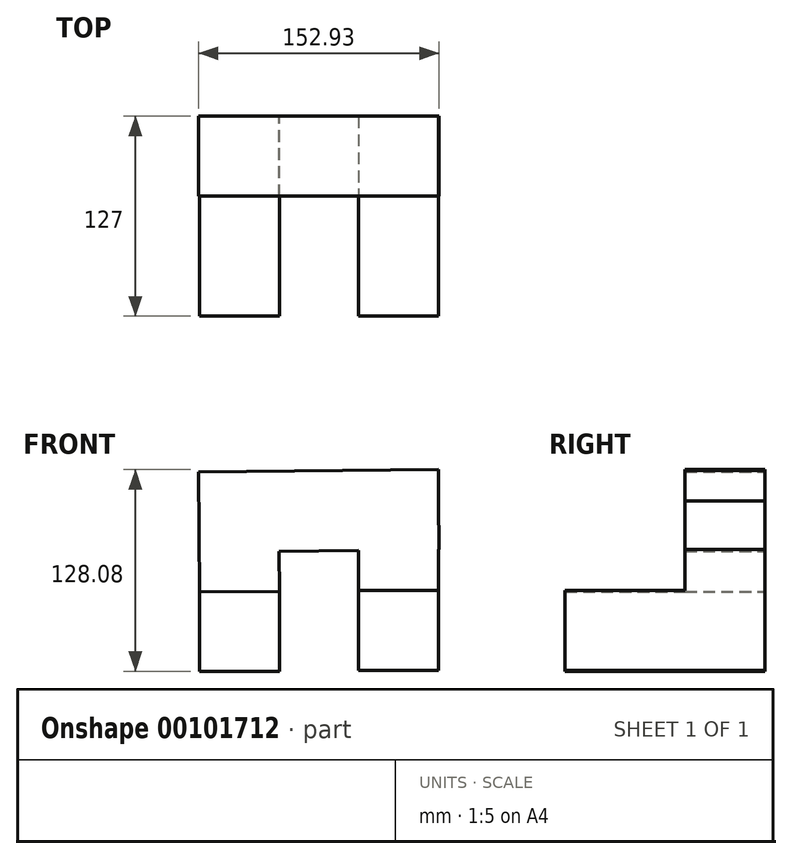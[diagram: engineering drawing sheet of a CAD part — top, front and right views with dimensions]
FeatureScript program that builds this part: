
annotation { "Feature Type Name" : "Feature", "Feature Type Description" : "" }
export const myFeature = defineFeature(function(context is Context, id is Id, definition is map)
    precondition{}
    {
        {
            var Q0;
            Q0=qCreatedBy(makeId("Front.planeOp"),FACE);
            var sketch = newSketch(context, id + "F0", { "sketchPlane" : qUnion([Q0])});
            skLineSegment(sketch, "E0", {"start": v(-79.81, 16.15) * mm, "end": v(-79.81, -34.1) * mm});
            skLineSegment(sketch, "E1", {"start": v(-79.81, -34.1) * mm, "end": v(-29.02, -34.1) * mm});
            skLineSegment(sketch, "E2", {"start": v(-29.02, -34.1) * mm, "end": v(-29.02, 16.7) * mm});
            skLineSegment(sketch, "E3", {"start": v(-29.02, 16.7) * mm, "end": v(-79.81, 16.15) * mm});
            skLineSegment(sketch, "E4", {"start": v(21.18, 17.14) * mm, "end": v(21.18, -33.66) * mm});
            skLineSegment(sketch, "E5", {"start": v(21.18, -33.66) * mm, "end": v(71.98, -33.66) * mm});
            skLineSegment(sketch, "E6", {"start": v(71.98, -33.66) * mm, "end": v(71.98, 17.14) * mm});
            skLineSegment(sketch, "E7", {"start": v(71.98, 17.14) * mm, "end": v(21.18, 17.14) * mm});
            skSolve(sketch);
        }
        {
            var Q0;
            Q0=makeQuery(id+"F0.imprint","IMPRINT",FACE,{"disambiguationData":[TD([[makeQuery(id+"F0.imprint","IMPRINT",EDGE,{"derivedFrom":sQuery(id+"F0.wireOp",EDGE,"E0")}),1.0]])]});
            extrude(context, id + "F1", {"entities" : qUnion([Q0]), "depth" : 127 * mm});
        }
        {
            var Q0;
            Q0=makeQuery(id+"F0.imprint","IMPRINT",FACE,{"disambiguationData":[TD([[makeQuery(id+"F0.imprint","IMPRINT",EDGE,{"derivedFrom":sQuery(id+"F0.wireOp",EDGE,"E4")}),1.0]])]});
            extrude(context, id + "F2", {"entities" : qUnion([Q0]), "depth" : 127 * mm});
        }
        {
            var Q0;
            Q0=makeQuery(id+"F1.opExtrude","SWEPT_FACE",FACE,{"disambiguationData":[OSD([sQuery(id+"F0.wireOp",EDGE,"E3")])]});
            var sketch = newSketch(context, id + "F3", { "sketchPlane" : qUnion([Q0])});
            skLineSegment(sketch, "E8.bottom", {"start": v(-79.64, 0) * mm, "end": v(-28.84, 0) * mm});
            skLineSegment(sketch, "E8.top", {"start": v(-79.64, -50.8) * mm, "end": v(-28.84, -50.8) * mm});
            skLineSegment(sketch, "E8.left", {"start": v(-79.64, 0) * mm, "end": v(-79.64, -50.8) * mm});
            skLineSegment(sketch, "E8.right", {"start": v(-28.84, 0) * mm, "end": v(-28.84, -50.8) * mm});
            skSolve(sketch);
        }
        {
            var Q0;
            Q0=makeQuery(id+"F3.imprint","IMPRINT",FACE,{"disambiguationData":[TD([[makeQuery(id+"F3.imprint","IMPRINT",EDGE,{"derivedFrom":sQuery(id+"F3.wireOp",EDGE,"E8.bottom")}),1.0]])]});
            extrude(context, id + "F4", {"entities" : qUnion([Q0]), "operationType" : NewBodyOperationType.ADD, "depth" : 76.2 * mm});
        }
        {
            var Q0;
            Q0=makeQuery(id+"F2.opExtrude","SWEPT_FACE",FACE,{"disambiguationData":[OSD([sQuery(id+"F0.wireOp",EDGE,"E7")])]});
            var sketch = newSketch(context, id + "F5", { "sketchPlane" : qUnion([Q0])});
            skLineSegment(sketch, "E9.bottom", {"start": v(21.18, 0) * mm, "end": v(71.98, 0) * mm});
            skLineSegment(sketch, "E9.top", {"start": v(21.18, -50.8) * mm, "end": v(71.98, -50.8) * mm});
            skLineSegment(sketch, "E9.left", {"start": v(21.18, 0) * mm, "end": v(21.18, -50.8) * mm});
            skLineSegment(sketch, "E9.right", {"start": v(71.98, 0) * mm, "end": v(71.98, -50.8) * mm});
            skSolve(sketch);
        }
        {
            var Q0;
            Q0=makeQuery(id+"F5.imprint","IMPRINT",FACE,{"disambiguationData":[TD([[makeQuery(id+"F5.imprint","IMPRINT",EDGE,{"derivedFrom":sQuery(id+"F5.wireOp",EDGE,"E9.bottom")}),1.0]])]});
            extrude(context, id + "F6", {"entities" : qUnion([Q0]), "operationType" : NewBodyOperationType.ADD, "depth" : 76.2 * mm});
        }
        {
            var Q0;
            Q0=makeQuery(id+"F4.opExtrude","SWEPT_FACE",FACE,{"disambiguationData":[OSD([sQuery(id+"F3.wireOp",EDGE,"E8.right")])]});
            var sketch = newSketch(context, id + "F7", { "sketchPlane" : qUnion([Q0])});
            skLineSegment(sketch, "E10.bottom", {"start": v(-50.8, 93.2) * mm, "end": v(0, 93.2) * mm});
            skLineSegment(sketch, "E10.top", {"start": v(-50.8, 42.4) * mm, "end": v(0, 42.4) * mm});
            skLineSegment(sketch, "E10.left", {"start": v(-50.8, 93.2) * mm, "end": v(-50.8, 42.4) * mm});
            skLineSegment(sketch, "E10.right", {"start": v(0, 93.2) * mm, "end": v(0, 42.4) * mm});
            skSolve(sketch);
        }
        {
            var Q0;
            Q0=makeQuery(id+"F7.imprint","IMPRINT",FACE,{"disambiguationData":[TD([[makeQuery(id+"F7.imprint","IMPRINT",EDGE,{"derivedFrom":sQuery(id+"F7.wireOp",EDGE,"E10.bottom")}),-1.0]])]});
            extrude(context, id + "F8", {"entities" : qUnion([Q0]), "operationType" : NewBodyOperationType.ADD, "depth" : 101.6 * mm});
        }
    });
